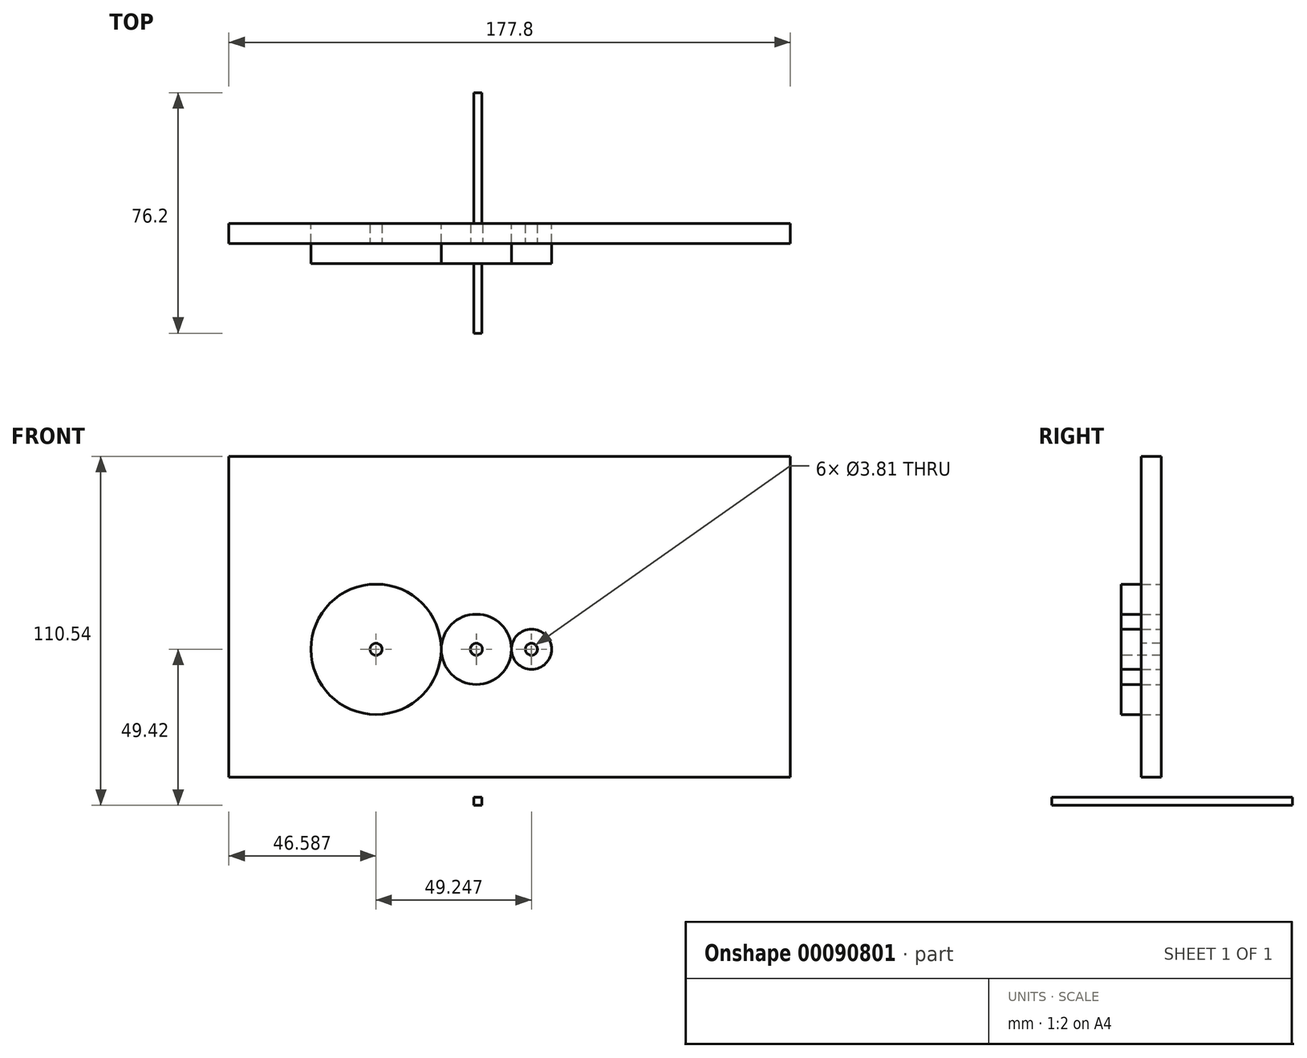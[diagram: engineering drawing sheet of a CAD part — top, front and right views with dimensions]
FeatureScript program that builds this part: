
annotation { "Feature Type Name" : "Feature", "Feature Type Description" : "" }
export const myFeature = defineFeature(function(context is Context, id is Id, definition is map)
    precondition{}
    {
        {
            var Q0;
            Q0=qCreatedBy(makeId("Front.planeOp"),FACE);
            var sketch = newSketch(context, id + "F0", { "sketchPlane" : qUnion([Q0])});
            skLineSegment(sketch, "E0.bottom", {"start": v(-77.52, 61.12) * mm, "end": v(100.28, 61.12) * mm});
            skLineSegment(sketch, "E0.top", {"start": v(-77.52, -40.48) * mm, "end": v(100.28, -40.48) * mm});
            skLineSegment(sketch, "E0.left", {"start": v(-77.52, 61.12) * mm, "end": v(-77.52, -40.48) * mm});
            skLineSegment(sketch, "E0.right", {"start": v(100.28, 61.12) * mm, "end": v(100.28, -40.48) * mm});
            skSolve(sketch);
        }
        {
            var Q0;
            Q0=makeQuery(id+"F0.imprint","IMPRINT",FACE,{"disambiguationData":[TD([[makeQuery(id+"F0.imprint","IMPRINT",EDGE,{"derivedFrom":sQuery(id+"F0.wireOp",EDGE,"E0.bottom")}),-1.0]])]});
            var sketch = newSketch(context, id + "F1", { "sketchPlane" : qUnion([Q0])});
            skCircle(sketch, "E1", {"center": v(-30.9, 0) * mm, "radius": 20.64 * mm});
            skCircle(sketch, "E2", {"center": v(0.85, 0) * mm, "radius": 11.11 * mm});
            skCircle(sketch, "E3", {"center": v(18.31, 0) * mm, "radius": 6.35 * mm});
            skSolve(sketch);
        }
        {
            var Q0;
            Q0=makeQuery(id+"F0.imprint","IMPRINT",FACE,{"disambiguationData":[TD([[makeQuery(id+"F0.imprint","IMPRINT",EDGE,{"derivedFrom":sQuery(id+"F0.wireOp",EDGE,"E0.bottom")}),-1.0]])]});
            extrude(context, id + "F2", {"entities" : qUnion([Q0]), "depth" : 6.35 * mm});
        }
        {
            var Q0;
            Q0 = qSketchRegion(id + "F1", true);
            extrude(context, id + "F3", {"entities" : qUnion([Q0]), "depth" : 12.7 * mm});
        }
        {
            var Q0;
            Q0=makeQuery(id+"F3.opExtrude","CAP_FACE",FACE,{"disambiguationData":[OSD([sQuery(id+"F1.wireOp",EDGE,"E1")])],"isStart":false});
            var sketch = newSketch(context, id + "F4", { "sketchPlane" : qUnion([Q0])});
            skCircle(sketch, "E4", {"center": v(-30.9, 0) * mm, "radius": 1.59 * mm});
            skSolve(sketch);
        }
        {
            var Q0;
            Q0=makeQuery(id+"F3.opExtrude","CAP_FACE",FACE,{"disambiguationData":[OSD([sQuery(id+"F1.wireOp",EDGE,"E3")])],"isStart":false});
            var sketch = newSketch(context, id + "F5", { "sketchPlane" : qUnion([Q0])});
            skCircle(sketch, "E5", {"center": v(18.31, 0) * mm, "radius": 1.59 * mm});
            skSolve(sketch);
        }
        {
            var Q0;
            Q0=makeQuery(id+"F3.opExtrude","CAP_FACE",FACE,{"disambiguationData":[OSD([sQuery(id+"F1.wireOp",EDGE,"E2")])],"isStart":false});
            var sketch = newSketch(context, id + "F6", { "sketchPlane" : qUnion([Q0])});
            skCircle(sketch, "E6", {"center": v(0.85, 0) * mm, "radius": 1.91 * mm});
            skSolve(sketch);
        }
        {
            var Q0;
            Q0=sQuery(id+"F4.wireOp",VERTEX,"E4.center");
            var Q1;
            Q1=makeQuery(id+"F3.opExtrude","SWEPT_BODY",BODY,{"disambiguationData":[OSD([sQuery(id+"F1.wireOp",EDGE,"E1")])]});
            hole(context, id + "F7", {"style" : HoleStyle.SIMPLE, "endStyle" : HoleEndStyle.THROUGH, "holeDiameter" : 3.8 * mm, "locations" : qUnion([Q0]), "scope" : qUnion([Q1]), "isTappedThrough" : true});
        }
        {
            var Q0;
            Q0=sQuery(id+"F6.wireOp",VERTEX,"E6.center");
            var Q1;
            Q1=makeQuery(id+"F3.opExtrude","SWEPT_BODY",BODY,{"disambiguationData":[OSD([sQuery(id+"F1.wireOp",EDGE,"E2")])]});
            hole(context, id + "F8", {"style" : HoleStyle.SIMPLE, "endStyle" : HoleEndStyle.THROUGH, "holeDiameter" : 3.8 * mm, "locations" : qUnion([Q0]), "scope" : qUnion([Q1]), "isTappedThrough" : true});
        }
        {
            var Q0;
            Q0=sQuery(id+"F5.wireOp",VERTEX,"E5.center");
            var Q1;
            Q1=makeQuery(id+"F3.opExtrude","SWEPT_BODY",BODY,{"disambiguationData":[OSD([sQuery(id+"F1.wireOp",EDGE,"E3")])]});
            hole(context, id + "F9", {"style" : HoleStyle.SIMPLE, "endStyle" : HoleEndStyle.THROUGH, "holeDiameter" : 3.8 * mm, "locations" : qUnion([Q0]), "scope" : qUnion([Q1]), "isTappedThrough" : true});
        }
        {
            var Q0;
            Q0=makeQuery(id+"F2.opExtrude","CAP_FACE",FACE,{"disambiguationData":[OSD([sQuery(id+"F0.wireOp",EDGE,"E0.bottom"),sQuery(id+"F0.wireOp",EDGE,"E0.top"),sQuery(id+"F0.wireOp",EDGE,"E0.left"),sQuery(id+"F0.wireOp",EDGE,"E0.right")])],"isStart":false});
            var sketch = newSketch(context, id + "F10", { "sketchPlane" : qUnion([Q0])});
            skCircle(sketch, "E7", {"center": v(-30.93, 0) * mm, "radius": 1.9 * mm});
            skSolve(sketch);
        }
        {
            var Q0;
            Q0=sQuery(id+"F10.wireOp",VERTEX,"E7.center");
            var Q1;
            Q1=makeQuery(id+"F2.opExtrude","SWEPT_BODY",BODY,{"disambiguationData":[OSD([sQuery(id+"F0.wireOp",EDGE,"E0.bottom"),sQuery(id+"F0.wireOp",EDGE,"E0.top"),sQuery(id+"F0.wireOp",EDGE,"E0.left"),sQuery(id+"F0.wireOp",EDGE,"E0.right")])]});
            hole(context, id + "F11", {"style" : HoleStyle.SIMPLE, "endStyle" : HoleEndStyle.THROUGH, "holeDiameter" : 3.8 * mm, "locations" : qUnion([Q0]), "scope" : qUnion([Q1]), "isTappedThrough" : true});
        }
        {
            var Q0;
            Q0=makeQuery(id+"F2.opExtrude","CAP_FACE",FACE,{"disambiguationData":[OSD([sQuery(id+"F0.wireOp",EDGE,"E0.bottom"),sQuery(id+"F0.wireOp",EDGE,"E0.top"),sQuery(id+"F0.wireOp",EDGE,"E0.left"),sQuery(id+"F0.wireOp",EDGE,"E0.right")])],"isStart":false});
            var sketch = newSketch(context, id + "F12", { "sketchPlane" : qUnion([Q0])});
            skCircle(sketch, "E8", {"center": v(0.89, 0) * mm, "radius": 1.9 * mm});
            skSolve(sketch);
        }
        {
            var Q0;
            Q0=sQuery(id+"F12.wireOp",VERTEX,"E8.center");
            var Q1;
            Q1=makeQuery(id+"F2.opExtrude","SWEPT_BODY",BODY,{"disambiguationData":[OSD([sQuery(id+"F0.wireOp",EDGE,"E0.bottom"),sQuery(id+"F0.wireOp",EDGE,"E0.top"),sQuery(id+"F0.wireOp",EDGE,"E0.left"),sQuery(id+"F0.wireOp",EDGE,"E0.right")])]});
            hole(context, id + "F13", {"style" : HoleStyle.SIMPLE, "endStyle" : HoleEndStyle.THROUGH, "holeDiameter" : 3.8 * mm, "locations" : qUnion([Q0]), "scope" : qUnion([Q1]), "isTappedThrough" : true});
        }
        {
            var Q0;
            Q0=makeQuery(id+"F2.opExtrude","CAP_FACE",FACE,{"disambiguationData":[OSD([sQuery(id+"F0.wireOp",EDGE,"E0.bottom"),sQuery(id+"F0.wireOp",EDGE,"E0.top"),sQuery(id+"F0.wireOp",EDGE,"E0.left"),sQuery(id+"F0.wireOp",EDGE,"E0.right")])],"isStart":false});
            var sketch = newSketch(context, id + "F14", { "sketchPlane" : qUnion([Q0])});
            skCircle(sketch, "E9", {"center": v(18.27, 0) * mm, "radius": 1.9 * mm});
            skSolve(sketch);
        }
        {
            var Q0;
            Q0=sQuery(id+"F14.wireOp",VERTEX,"E9.center");
            var Q1;
            Q1=makeQuery(id+"F2.opExtrude","SWEPT_BODY",BODY,{"disambiguationData":[OSD([sQuery(id+"F0.wireOp",EDGE,"E0.bottom"),sQuery(id+"F0.wireOp",EDGE,"E0.top"),sQuery(id+"F0.wireOp",EDGE,"E0.left"),sQuery(id+"F0.wireOp",EDGE,"E0.right")])]});
            hole(context, id + "F15", {"style" : HoleStyle.SIMPLE, "endStyle" : HoleEndStyle.THROUGH, "holeDiameter" : 3.8 * mm, "locations" : qUnion([Q0]), "scope" : qUnion([Q1]), "isTappedThrough" : true});
        }
        {
            var Q0;
            Q0=qCreatedBy(makeId("Right.planeOp"),FACE);
            var sketch = newSketch(context, id + "F16", { "sketchPlane" : qUnion([Q0])});
            skLineSegment(sketch, "E10.bottom", {"start": v(41.45, -46.88) * mm, "end": v(-34.75, -46.88) * mm});
            skLineSegment(sketch, "E10.top", {"start": v(41.45, -49.42) * mm, "end": v(-34.75, -49.42) * mm});
            skLineSegment(sketch, "E10.left", {"start": v(41.45, -46.88) * mm, "end": v(41.45, -49.42) * mm});
            skLineSegment(sketch, "E10.right", {"start": v(-34.75, -46.88) * mm, "end": v(-34.75, -49.42) * mm});
            skSolve(sketch);
        }
        {
            var Q0;
            Q0=makeQuery(id+"F16.imprint","IMPRINT",FACE,{"disambiguationData":[TD([[makeQuery(id+"F16.imprint","IMPRINT",EDGE,{"derivedFrom":sQuery(id+"F16.wireOp",EDGE,"E10.bottom")}),1.0]])]});
            extrude(context, id + "F17", {"entities" : qUnion([Q0]), "depth" : 2.54 * mm});
        }
    });
